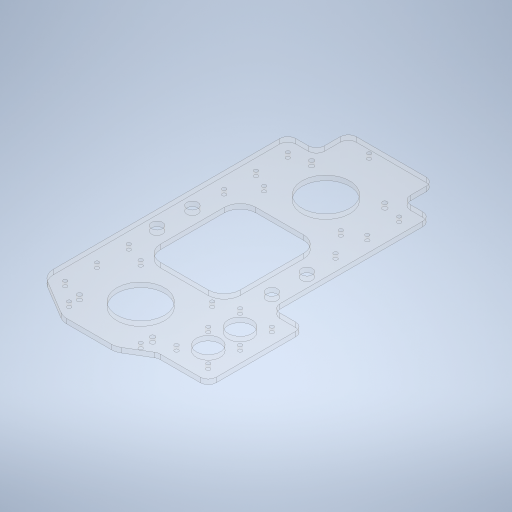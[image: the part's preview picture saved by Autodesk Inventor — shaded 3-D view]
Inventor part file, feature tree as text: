
AUTODESK INVENTOR PART (.ipt)
format: ipt  version: 2023 (Build 270158000, 158)  size: 462,336 bytes
history: native  units: in
note: dims shown in document units (in); Inventor stores cm internally (conversion verified against a paired STEP export)
features: extrude x1
ambient origin geometry x8: Origin, YZ Plane, XZ Plane, XY Plane, X Axis, Y Axis, Z Axis, Center Point
bodies: Body1 (feature_tree)
feature tree (1):
  extrude  "Extrusion2"  Depth=3.5433in
